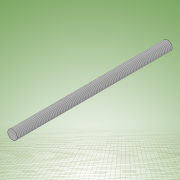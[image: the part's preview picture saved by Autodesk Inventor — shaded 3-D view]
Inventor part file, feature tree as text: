
AUTODESK INVENTOR PART (.ipt)
format: ipt  version: 2022 (Build 260153000, 153)  size: 109,568 bytes
history: native  units: mm
features: other x1, extrude x1, thread x1, sketch x1
ambient origin geometry x8: Origin, YZ Plane, XZ Plane, XY Plane, X Axis, Y Axis, Z Axis, Center Point
bodies: Body1 (feature_tree)
feature tree (4):
  other  "Sólido1"
  extrude  "Extrusión1"  Depth=100.0mm TaperAngle=0.0deg
  thread  "Rosca1"  [1 undecoded]
  sketch  "Boceto1"  dims[d0=6.096mm d1=100.0mm d2=0.0mm d3=100.0mm d4=0.0mm]
note: 1 required parameter value undecoded (feature->parameter linkage not recoverable at this tier; creation-order binding heuristic only, values carry confidence <= 0.55)
